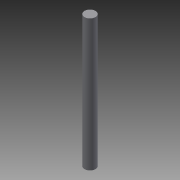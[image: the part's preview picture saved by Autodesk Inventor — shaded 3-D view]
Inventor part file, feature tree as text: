
AUTODESK INVENTOR PART (.ipt)
format: ipt  version: 2015 (Build 190159000, 159)  size: 63,488 bytes
history: native  units: in
note: dims shown in document units (in); Inventor stores cm internally (conversion verified against a paired STEP export)
features: extrude x1, sketch x1
ambient origin geometry x8: Origin, YZ Plane, XZ Plane, XY Plane, X Axis, Y Axis, Z Axis, Center Point
bodies: Solid1 (feature_tree)
feature tree (2):
  extrude  "Extrusion1"  Depth=3.5in TaperAngle=0.0deg
  sketch  "Sketch1"  dims[d0=0.25in d1=3.5in d2=0.0in]
